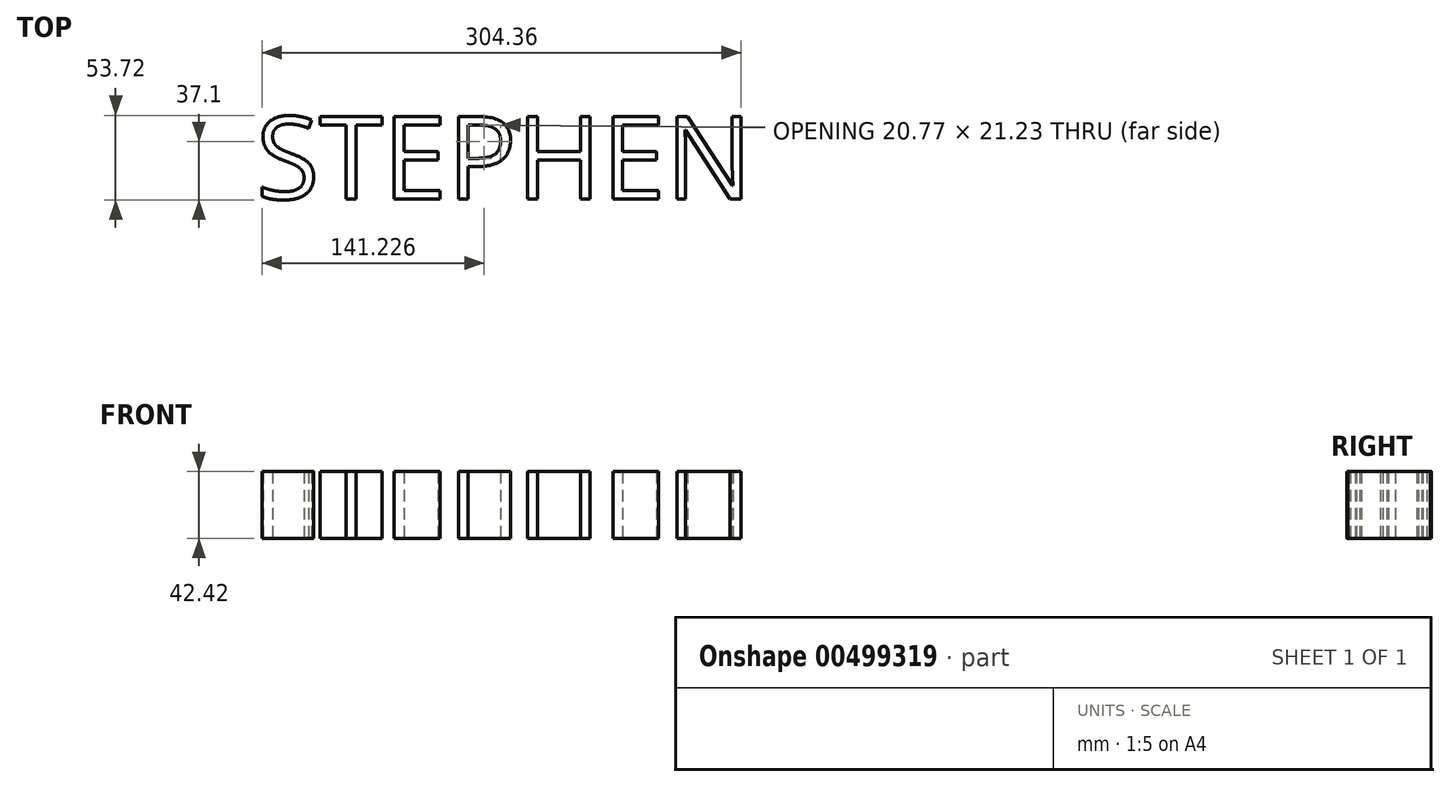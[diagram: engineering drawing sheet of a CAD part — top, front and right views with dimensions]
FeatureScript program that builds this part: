
annotation { "Feature Type Name" : "Feature", "Feature Type Description" : "" }
export const myFeature = defineFeature(function(context is Context, id is Id, definition is map)
    precondition{}
    {
        {
            var Q0;
            Q0=qCreatedBy(makeId("Top.planeOp"),FACE);
            var sketch = newSketch(context, id + "F0", { "sketchPlane" : qUnion([Q0])});
            skText(sketch, "E0", { "text": "STEPHEN", "fontName": "OpenSans-Regular.ttf"});
            const initialGuessF0  = {"E0": [-0.0764, -0.00209, 1, 0, 0.0527]};
            skSetInitialGuess(sketch, initialGuessF0);
            skSolve(sketch);
        }
        {
            var Q0;
            Q0 = qSketchRegion(id + "F0", true);
            extrude(context, id + "F1", {"entities" : qUnion([Q0]), "depth" : 42.42 * mm});
        }
    });
